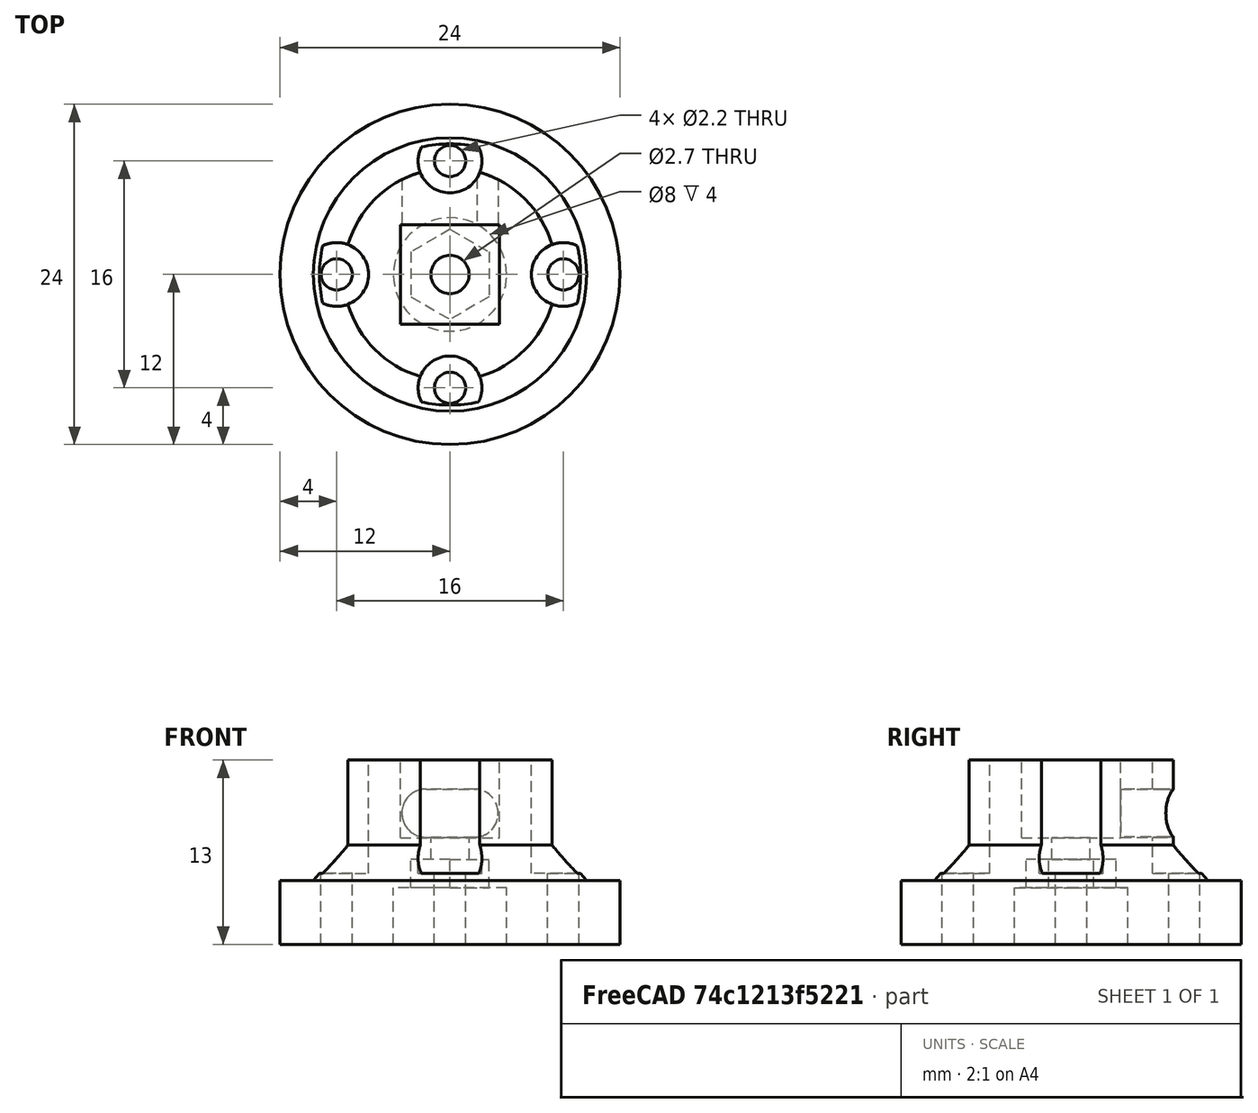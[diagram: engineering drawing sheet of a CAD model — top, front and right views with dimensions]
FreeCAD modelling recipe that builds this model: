
FCSTD DOCUMENT  (FreeCAD 0.15R4671 (Git))
Label: tendon_wheel_pwm_fingers
License: CC-BY 3.0
LicenseURL: http://creativecommons.org/licenses/by/3.0/
objects: Part::Cylinder×14, Part::MultiFuse×6, Part::Box×2, Part::Cone×1, Part::Extrusion×1, Part::Mirroring×1, Part::Cut×1
note: 26 computed .brp shape members not serialized (recipe doc carries the construction recipe); baked Part::Feature solids carry a one-line shape summary decoded from their .brp

FEATURE [Part::Cylinder] Cylinder
  Angle = 360
  Height = 4.5
  Placement = pos=(0,0,0.5) rot=(0,0,1;0rad)
  Radius = 12
FEATURE [Part::Cone] Cone
  Angle = 360
  Height = 3.5
  Placement = pos=(0,0,4) rot=(0,0,1;0rad)
  Radius1 = 10.5
  Radius2 = 7.5
FEATURE [Part::Cylinder] Cylinder001
  Angle = 360
  Height = 6.5
  Placement = pos=(0,0,7) rot=(0,0,1;0rad)
  Radius = 7.5
FEATURE [Part::Cylinder] Cylinder003  label="TopHole003"
  Angle = 360
  Height = 20
  Placement = pos=(-8,0,-3) rot=(0,0,1;0rad)
  Radius = 1.1
FEATURE [Part::Cylinder] Cylinder004  label="TopHole002"
  Angle = 360
  Height = 20
  Placement = pos=(0,-8,-3) rot=(0,0,1;0rad)
  Radius = 1.1
FEATURE [Part::Cylinder] Cylinder005  label="TopHole001"
  Angle = 360
  Height = 20
  Placement = pos=(8,0,-3) rot=(0,0,1;0rad)
  Radius = 1.1
FEATURE [Part::Cylinder] Cylinder006  label="TopHole"
  Angle = 360
  Height = 10
  Placement = pos=(0,8,-3) rot=(0,0,1;0rad)
  Radius = 1.1
FEATURE [Part::Cylinder] Cylinder007  label="TopHole004"
  Angle = 360
  Height = 20
  Placement = pos=(-8,0,3.5) rot=(0,0,1;0rad)
  Radius = 2.25
FEATURE [Part::Cylinder] Cylinder008  label="TopHole005"
  Angle = 360
  Height = 20
  Placement = pos=(8,0,3.5) rot=(0,0,1;0rad)
  Radius = 2.25
FEATURE [Part::Cylinder] Cylinder009  label="TopHole006"
  Angle = 360
  Height = 20
  Placement = pos=(0,8,3.5) rot=(0,0,1;0rad)
  Radius = 2.25
FEATURE [Part::Cylinder] Cylinder010  label="TopHole007"
  Angle = 360
  Height = 20
  Placement = pos=(0,-8,3.5) rot=(0,0,1;0rad)
  Radius = 2.25
FEATURE [Part::MultiFuse] Fusion001
  Placement = pos=(0,0,2) rot=(0,0,1;0rad)
  Shapes = -> [Cylinder010,Cylinder007,Cylinder005,Cylinder003,Cylinder009,Cylinder004,Cylinder008,Cylinder006]
FEATURE [Part::Cylinder] Cylinder012  label="Cylinder003"
  Angle = 360
  Height = 10
  Placement = pos=(-1.7,12,9.75) rot=(1,0,0;1.5708rad)
  Radius = 1.7
FEATURE [Part::Cylinder] Cylinder013  label="Cylinder004"
  Angle = 360
  Height = 20
  Placement = pos=(0,0,-5) rot=(0,0,1;0rad)
  Radius = 1.35
FEATURE [Part::Box] Box  label="Cube"
  Height = 8
  Length = 7
  Placement = pos=(-3.5,-3.5,8) rot=(0,0,1;0rad)
  Width = 7
FEATURE [Part::Extrusion] Extrude
  Dir = (0,0,2)
  Solid = true
FEATURE [Part::Mirroring] Part__Mirroring  label="Extrude (Mirror #1)"
  Base = (0,0,0)
  Normal = (1,0,0)
  Source = -> Extrude
FEATURE [Part::MultiFuse] Fusion002
  Placement = pos=(0,0,4.5) rot=(0,0,1;0rad)
  Shapes = -> [Part__Mirroring,Extrude]
FEATURE [Part::Cylinder] Cylinder014  label="Cylinder005"
  Angle = 360
  Height = 4.5
  Radius = 4
FEATURE [Part::Cylinder] Cylinder015  label="Cylinder006"
  Angle = 360
  Height = 10
  Placement = pos=(1.7,12,9.75) rot=(1,0,0;1.5708rad)
  Radius = 1.7
FEATURE [Part::Box] Box001  label="Cube001"
  Height = 3.4
  Length = 3.6
  Placement = pos=(-1.7,2,8.05) rot=(0,0,1;0rad)
  Width = 10
FEATURE [Part::MultiFuse] Fusion
  Shapes = -> [Cylinder,Cone,Cylinder001]
FEATURE [Part::MultiFuse] Fusion005
  Shapes = -> [Cylinder014,Fusion002,Cylinder013,Fusion001]
FEATURE [Part::MultiFuse] Fusion006
  Shapes = -> [Cylinder015,Box001,Cylinder012,Box]
FEATURE [Part::MultiFuse] Fusion007
  Shapes = -> [Fusion006,Fusion005]
FEATURE [Part::Cut] Cut
  Base = -> Fusion
  Tool = -> Fusion007
